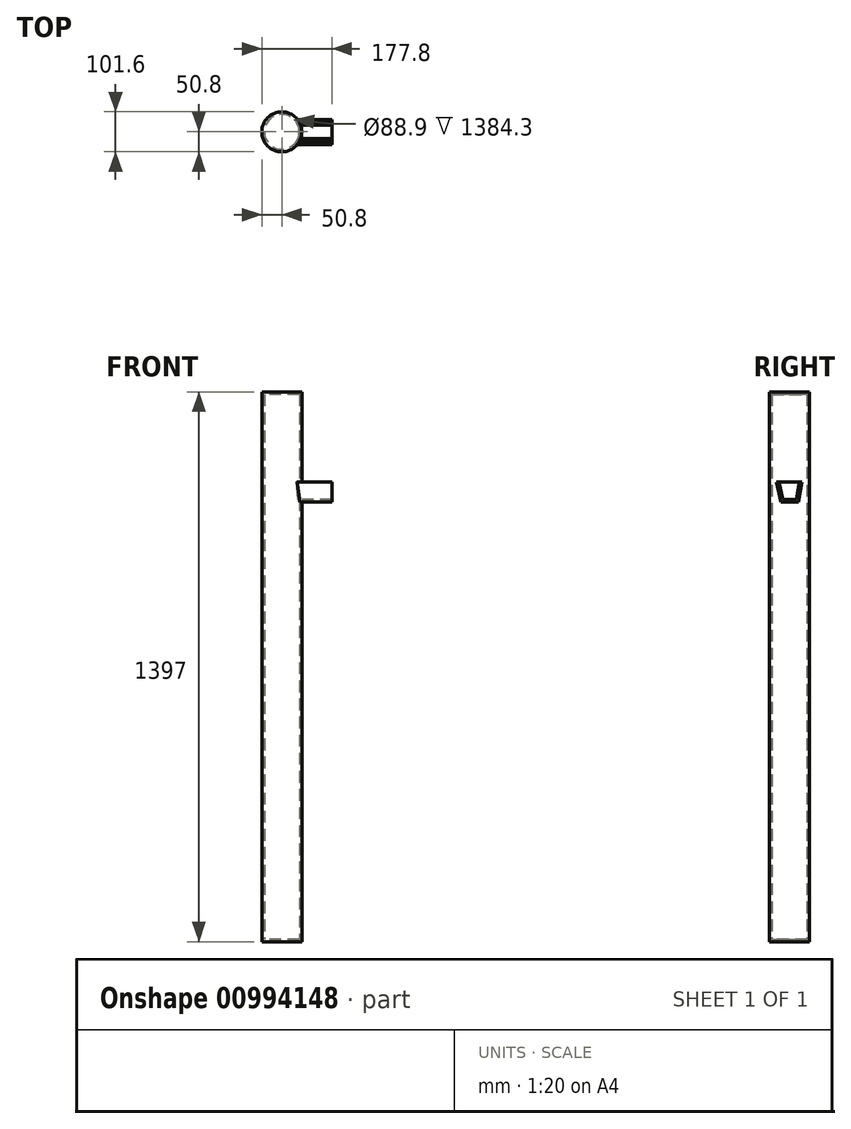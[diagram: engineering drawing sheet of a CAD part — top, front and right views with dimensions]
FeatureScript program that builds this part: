
annotation { "Feature Type Name" : "Feature", "Feature Type Description" : "" }
export const myFeature = defineFeature(function(context is Context, id is Id, definition is map)
    precondition{}
    {
        {
            var Q0;
            Q0=qCreatedBy(makeId("Top.planeOp"),FACE);
            var sketch = newSketch(context, id + "F0", { "sketchPlane" : qUnion([Q0])});
            skCircle(sketch, "E0", {"center": v(0, 0) * mm, "radius": 50.8 * mm});
            skSolve(sketch);
        }
        {
            var Q0;
            Q0 = qSketchRegion(id + "F0", true);
            extrude(context, id + "F1", {"entities" : qUnion([Q0]), "depth" : 1397 * mm, "offsetDistance" : 25.4 * mm});
        }
        {
            var Q0;
            Q0=qCreatedBy(makeId("Right.planeOp"),FACE);
            var sketch = newSketch(context, id + "F2", { "sketchPlane" : qUnion([Q0])});
            skLineSegment(sketch, "E1", {"start": v(-33.02, 1168.4) * mm, "end": v(-22.23, 1117.6) * mm});
            skLineSegment(sketch, "E2", {"start": v(-22.23, 1117.6) * mm, "end": v(22.23, 1117.6) * mm});
            skLineSegment(sketch, "E3", {"start": v(22.23, 1117.6) * mm, "end": v(31.18, 1168.4) * mm});
            skLineSegment(sketch, "E4", {"start": v(-33.02, 1168.4) * mm, "end": v(31.18, 1168.4) * mm});
            skPoint(sketch, "E5", {"position": v(0, 1117.6) * mm});
            skSolve(sketch);
        }
        {
            var Q0;
            Q0 = qSketchRegion(id + "F2", true);
            extrude(context, id + "F3", {"entities" : qUnion([Q0]), "operationType" : NewBodyOperationType.ADD, "depth" : 127 * mm, "offsetDistance" : 25.4 * mm});
        }
        {
            var Q0;
            Q0=makeQuery(id+"F3.opExtrude","SWEPT_FACE",FACE,{"disambiguationData":[OSD([sQuery(id+"F2.wireOp",EDGE,"E4")])]});
            var Q1;
            Q1=makeQuery(id+"F3.opExtrude","CAP_FACE",FACE,{"disambiguationData":[OSD([sQuery(id+"F2.wireOp",EDGE,"E1"),sQuery(id+"F2.wireOp",EDGE,"E2"),sQuery(id+"F2.wireOp",EDGE,"E3"),sQuery(id+"F2.wireOp",EDGE,"E4")])],"isStart":false});
            shell(context, id + "F4", {"entities" : qUnion([Q0, Q1]), "thickness" : 6.35 * mm});
        }
    });
